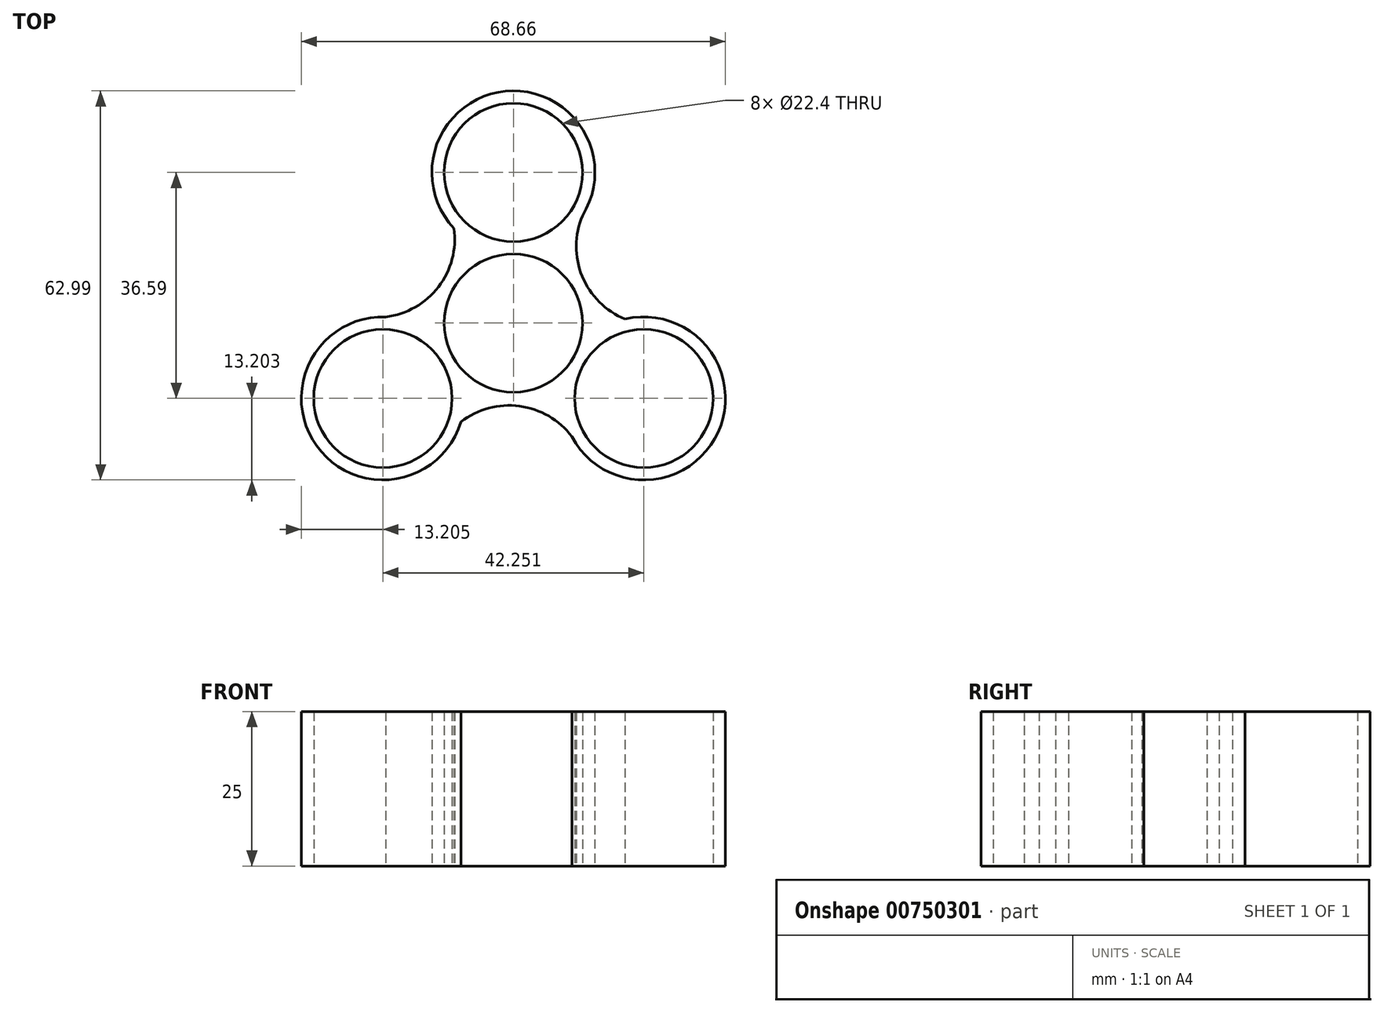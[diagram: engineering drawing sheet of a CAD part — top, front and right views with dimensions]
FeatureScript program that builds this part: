
annotation { "Feature Type Name" : "Feature", "Feature Type Description" : "" }
export const myFeature = defineFeature(function(context is Context, id is Id, definition is map)
    precondition{}
    {
        {
            var Q0;
            Q0=qCreatedBy(makeId("Top.planeOp"),FACE);
            var sketch = newSketch(context, id + "F0", { "sketchPlane" : qUnion([Q0])});
            skCircle(sketch, "E0", {"center": v(0, 0) * mm, "radius": 11.2 * mm});
            skCircle(sketch, "E1", {"center": v(0, 24.4) * mm, "radius": 13.2 * mm});
            skCircle(sketch, "E2", {"center": v(0, 24.4) * mm, "radius": 11.2 * mm});
            skCircle(sketch, "E3.1.0", {"center": v(-21.13, -12.2) * mm, "radius": 13.2 * mm});
            skCircle(sketch, "E3.2.0", {"center": v(21.13, -12.2) * mm, "radius": 13.2 * mm});
            skCircle(sketch, "E4.1.0", {"center": v(-21.13, -12.2) * mm, "radius": 11.2 * mm});
            skCircle(sketch, "E4.2.0", {"center": v(21.13, -12.2) * mm, "radius": 11.2 * mm});
            skArc(sketch, "E5", {"start": v(11.18, 17.38) * mm, "mid": v(11.14, 7.57) * mm, "end": v(18.09, 0.65) * mm});
            skArc(sketch, "E6.1.0", {"start": v(-20.65, 1) * mm, "mid": v(-12.13, 5.86) * mm, "end": v(-9.6, 15.34) * mm});
            skArc(sketch, "E6.2.0", {"start": v(9.46, -18.38) * mm, "mid": v(0.99, -13.44) * mm, "end": v(-8.48, -15.99) * mm});
            skSolve(sketch);
        }
        {
            var Q0;
            Q0 = qSketchRegion(id + "F0", true);
            extrude(context, id + "F1", {"entities" : qUnion([Q0]), "depth" : 25 * mm, "offsetDistance" : 25 * mm});
        }
    });
